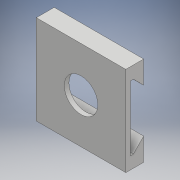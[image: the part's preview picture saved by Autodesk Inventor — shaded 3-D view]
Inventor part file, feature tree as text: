
AUTODESK INVENTOR PART (.ipt)
format: ipt  version: 2017 (Build 210142000, 142)  size: 113,152 bytes
history: native  units: mm
features: extrude x2, hole x1, sketch x1
ambient origin geometry x8: Origin, YZ Plane, XZ Plane, XY Plane, X Axis, Y Axis, Z Axis, Center Point
bodies: Solid1 (feature_tree)
feature tree (4):
  extrude  "Block"  Depth=12.0mm
  extrude  "Tripod Slot"  Depth=60.0mm TaperAngle=0.0deg
  hole  "Hole1"  [1 undecoded]
  sketch  "Sketch2"  dims[d0=60.0mm d1=12.0mm d14=60.0mm d15=0.0mm d17=14.75mm d18=14.75mm d19=8.9mm d20=21.75mm d21=21.75mm d22=2.0mm d23=2.0mm d24=60.0mm d25=0.0mm d46=30.0mm d47=30.0mm d48=22.5mm d49=6.0mm d50=4.0mm d51=2.0mm d52=90.0deg d53=8.0mm d54=20.594885mm]
note: 1 required parameter value undecoded (feature->parameter linkage not recoverable at this tier; creation-order binding heuristic only, values carry confidence <= 0.55)
